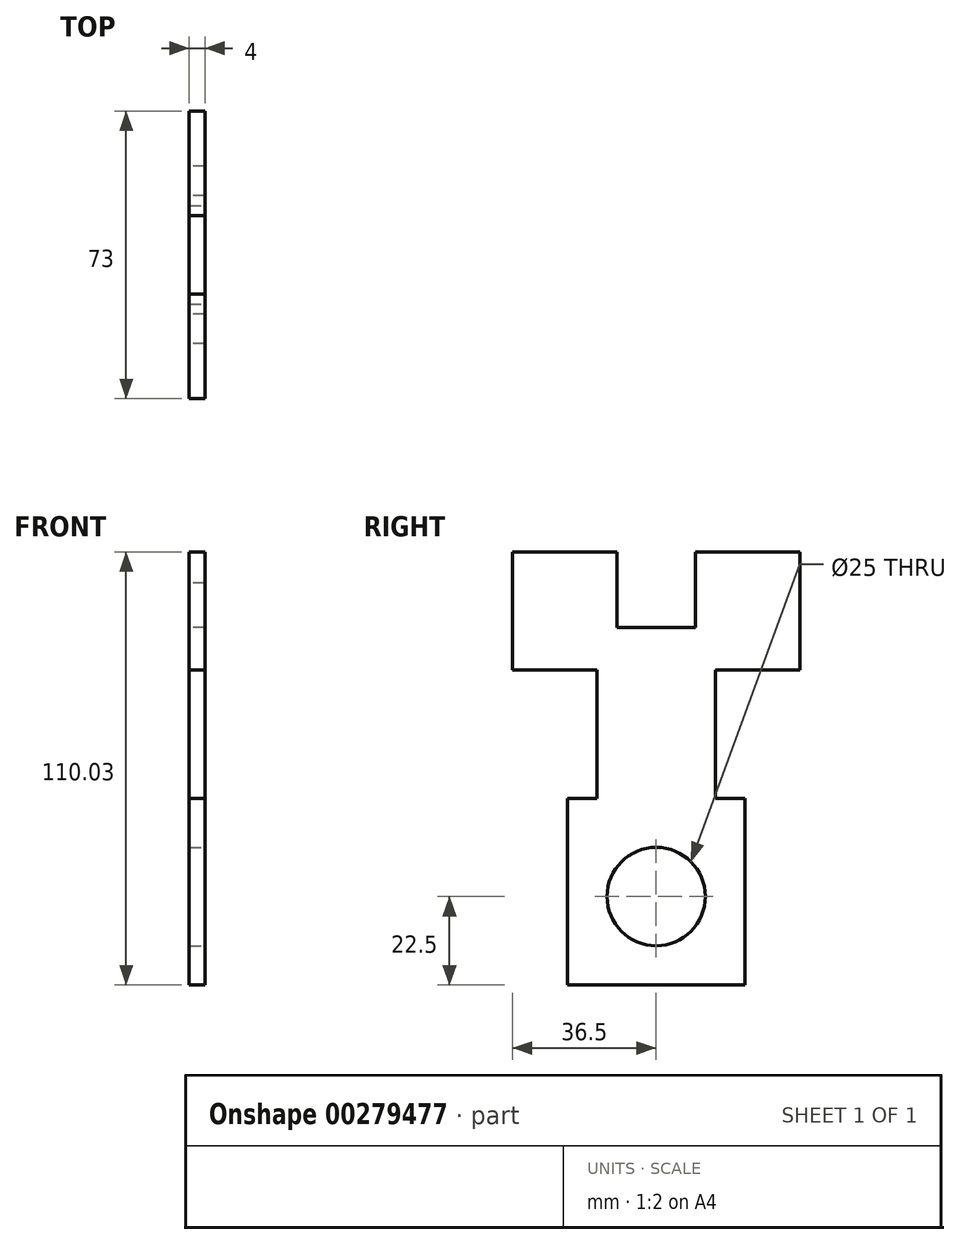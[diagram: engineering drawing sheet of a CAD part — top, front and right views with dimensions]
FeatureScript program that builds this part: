
annotation { "Feature Type Name" : "Feature", "Feature Type Description" : "" }
export const myFeature = defineFeature(function(context is Context, id is Id, definition is map)
    precondition{}
    {
        {
            var Q0;
            Q0=qCreatedBy(makeId("Right.planeOp"),FACE);
            var sketch = newSketch(context, id + "F0", { "sketchPlane" : qUnion([Q0])});
            skLineSegment(sketch, "E0.bottom", {"start": v(-36.5, 53.04) * mm, "end": v(-10, 53.04) * mm});
            skLineSegment(sketch, "E0.top", {"start": v(-36.5, 23.04) * mm, "end": v(-15, 23.04) * mm});
            skLineSegment(sketch, "E0.left", {"start": v(-36.5, 53.04) * mm, "end": v(-36.5, 23.04) * mm});
            skLineSegment(sketch, "E0.right", {"start": v(36.5, 53.04) * mm, "end": v(36.5, 23.04) * mm});
            skLineSegment(sketch, "E1.top", {"start": v(-15, -56.96) * mm, "end": v(15, -56.96) * mm});
            skLineSegment(sketch, "E1.left", {"start": v(-15, 23.04) * mm, "end": v(-15, 0) * mm});
            skLineSegment(sketch, "E1.right", {"start": v(15, 23.04) * mm, "end": v(15, 0) * mm});
            skLineSegment(sketch, "E2.trimOffspring", {"start": v(15, 23.04) * mm, "end": v(36.5, 23.04) * mm});
            skLineSegment(sketch, "E3.top", {"start": v(9.95, 45.14) * mm, "end": v(10, 45.14) * mm});
            skLineSegment(sketch, "E3.left", {"start": v(-10, 53.04) * mm, "end": v(-10, 45.14) * mm});
            skLineSegment(sketch, "E3.right", {"start": v(10, 53.04) * mm, "end": v(10, 45.14) * mm});
            skLineSegment(sketch, "E4.trimOffspring", {"start": v(10, 53.04) * mm, "end": v(36.5, 53.04) * mm});
            skLineSegment(sketch, "E5.top", {"start": v(-10, 33.91) * mm, "end": v(9.95, 33.91) * mm});
            skLineSegment(sketch, "E5.left", {"start": v(-10, 45.14) * mm, "end": v(-10, 33.91) * mm});
            skLineSegment(sketch, "E5.right", {"start": v(9.95, 45.14) * mm, "end": v(9.95, 33.91) * mm});
            skLineSegment(sketch, "E6.top", {"start": v(0, -57) * mm, "end": v(22.5, -57) * mm});
            skLineSegment(sketch, "E6.left", {"start": v(0, -56.96) * mm, "end": v(0, -57) * mm});
            skLineSegment(sketch, "E6.right", {"start": v(22.5, -9.62) * mm, "end": v(22.5, -57) * mm});
            skLineSegment(sketch, "E7.top", {"start": v(0, -57) * mm, "end": v(-22.5, -57) * mm});
            skLineSegment(sketch, "E7.right", {"start": v(-22.5, -9.62) * mm, "end": v(-22.5, -57) * mm});
            skLineSegment(sketch, "E8", {"start": v(-22.5, -9.62) * mm, "end": v(-15, -9.62) * mm});
            skLineSegment(sketch, "E9", {"start": v(-15, 0) * mm, "end": v(-15, -9.62) * mm});
            skLineSegment(sketch, "E10", {"start": v(15, 0) * mm, "end": v(15, -9.62) * mm});
            skLineSegment(sketch, "E11.trimOffspring", {"start": v(15, -9.62) * mm, "end": v(22.5, -9.62) * mm});
            skSolve(sketch);
        }
        {
            var Q0;
            Q0=makeQuery(id+"F0.imprint","IMPRINT",FACE,{"disambiguationData":[TD([[makeQuery(id+"F0.imprint","IMPRINT",EDGE,{"derivedFrom":sQuery(id+"F0.wireOp",EDGE,"E0.bottom")}),-1.0]])]});
            extrude(context, id + "F1", {"entities" : qUnion([Q0]), "depth" : 4 * mm, "offsetDistance" : 25 * mm});
        }
        {
            var Q0;
            Q0=makeQuery(id+"F1.opExtrude","CAP_FACE",FACE,{"disambiguationData":[OSD([sQuery(id+"F0.wireOp",EDGE,"E0.bottom"),sQuery(id+"F0.wireOp",EDGE,"E0.top"),sQuery(id+"F0.wireOp",EDGE,"E0.left"),sQuery(id+"F0.wireOp",EDGE,"E0.right"),sQuery(id+"F0.wireOp",EDGE,"E1.left"),sQuery(id+"F0.wireOp",EDGE,"E1.right"),sQuery(id+"F0.wireOp",EDGE,"E2.trimOffspring"),sQuery(id+"F0.wireOp",EDGE,"E3.top"),sQuery(id+"F0.wireOp",EDGE,"E3.left"),sQuery(id+"F0.wireOp",EDGE,"E3.right"),sQuery(id+"F0.wireOp",EDGE,"E4.trimOffspring"),sQuery(id+"F0.wireOp",EDGE,"E5.top"),sQuery(id+"F0.wireOp",EDGE,"E5.left"),sQuery(id+"F0.wireOp",EDGE,"E5.right"),sQuery(id+"F0.wireOp",EDGE,"E6.top"),sQuery(id+"F0.wireOp",EDGE,"E6.right"),sQuery(id+"F0.wireOp",EDGE,"E7.top"),sQuery(id+"F0.wireOp",EDGE,"E7.right"),sQuery(id+"F0.wireOp",EDGE,"E8"),sQuery(id+"F0.wireOp",EDGE,"E9"),sQuery(id+"F0.wireOp",EDGE,"E10"),sQuery(id+"F0.wireOp",EDGE,"E11.trimOffspring")])],"isStart":false});
            var sketch = newSketch(context, id + "F2", { "sketchPlane" : qUnion([Q0])});
            skCircle(sketch, "E12", {"center": v(0, -34.5) * mm, "radius": 12.5 * mm});
            skSolve(sketch);
        }
        {
            var Q0;
            Q0=makeQuery(id+"F2.imprint","IMPRINT",FACE,{"disambiguationData":[TD([[makeQuery(id+"F2.imprint","IMPRINT",EDGE,{"derivedFrom":sQuery(id+"F2.wireOp",EDGE,"E12")}),1.0]])]});
            extrude(context, id + "F3", {"entities" : qUnion([Q0]), "operationType" : NewBodyOperationType.REMOVE, "oppositeDirection" : true, "depth" : 25 * mm, "offsetDistance" : 25 * mm});
        }
    });
